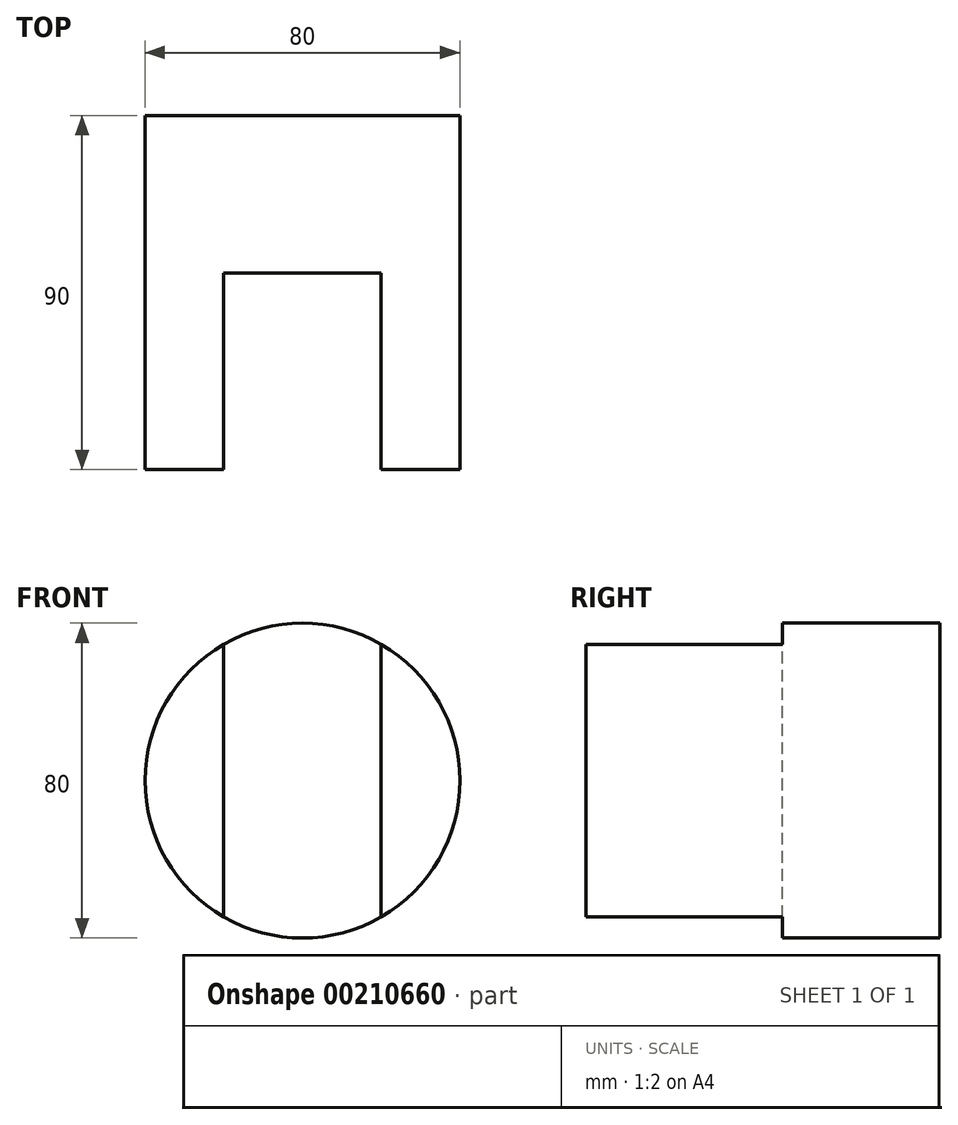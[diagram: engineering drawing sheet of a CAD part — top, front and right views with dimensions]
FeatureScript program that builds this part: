
annotation { "Feature Type Name" : "Feature", "Feature Type Description" : "" }
export const myFeature = defineFeature(function(context is Context, id is Id, definition is map)
    precondition{}
    {
        {
            var Q0;
            Q0=qCreatedBy(makeId("Front.planeOp"),FACE);
            var sketch = newSketch(context, id + "F0", { "sketchPlane" : qUnion([Q0])});
            skCircle(sketch, "E0", {"center": v(0, 0) * mm, "radius": 40 * mm});
            skSolve(sketch);
        }
        {
            var Q0;
            Q0=makeQuery(id+"F0.imprint","IMPRINT",FACE,{"disambiguationData":[TD([[makeQuery(id+"F0.imprint","IMPRINT",EDGE,{"derivedFrom":sQuery(id+"F0.wireOp",EDGE,"E0")}),1.0]])]});
            extrude(context, id + "F1", {"entities" : qUnion([Q0]), "depth" : 90 * mm});
        }
        {
            var Q0;
            Q0=makeQuery(id+"F1.opExtrude","CAP_FACE",FACE,{"disambiguationData":[OSD([sQuery(id+"F0.wireOp",EDGE,"E0")])],"isStart":false});
            var sketch = newSketch(context, id + "F2", { "sketchPlane" : qUnion([Q0])});
            skLineSegment(sketch, "E1", {"start": v(-20, 0) * mm, "end": v(-20, -34.64) * mm});
            skLineSegment(sketch, "E2", {"start": v(-20, 0) * mm, "end": v(-20, 34.64) * mm});
            skLineSegment(sketch, "E3", {"start": v(20, 0) * mm, "end": v(20, 34.64) * mm});
            skLineSegment(sketch, "E4", {"start": v(20, 34.64) * mm, "end": v(20, -34.64) * mm});
            skArc(sketch, "E5", {"start": v(-20, 34.64) * mm, "mid": v(0, 40) * mm, "end": v(20, 34.64) * mm});
            skArc(sketch, "E6", {"start": v(-20, -34.64) * mm, "mid": v(0, -40) * mm, "end": v(20, -34.64) * mm});
            skSolve(sketch);
        }
        {
            var Q0;
            Q0=makeQuery(id+"F2.imprint","IMPRINT",FACE,{"disambiguationData":[TD([[makeQuery(id+"F2.imprint","IMPRINT",EDGE,{"derivedFrom":sQuery(id+"F2.wireOp",EDGE,"E1")}),1.0]])]});
            extrude(context, id + "F3", {"entities" : qUnion([Q0]), "operationType" : NewBodyOperationType.REMOVE, "oppositeDirection" : true, "depth" : 50 * mm});
        }
    });
